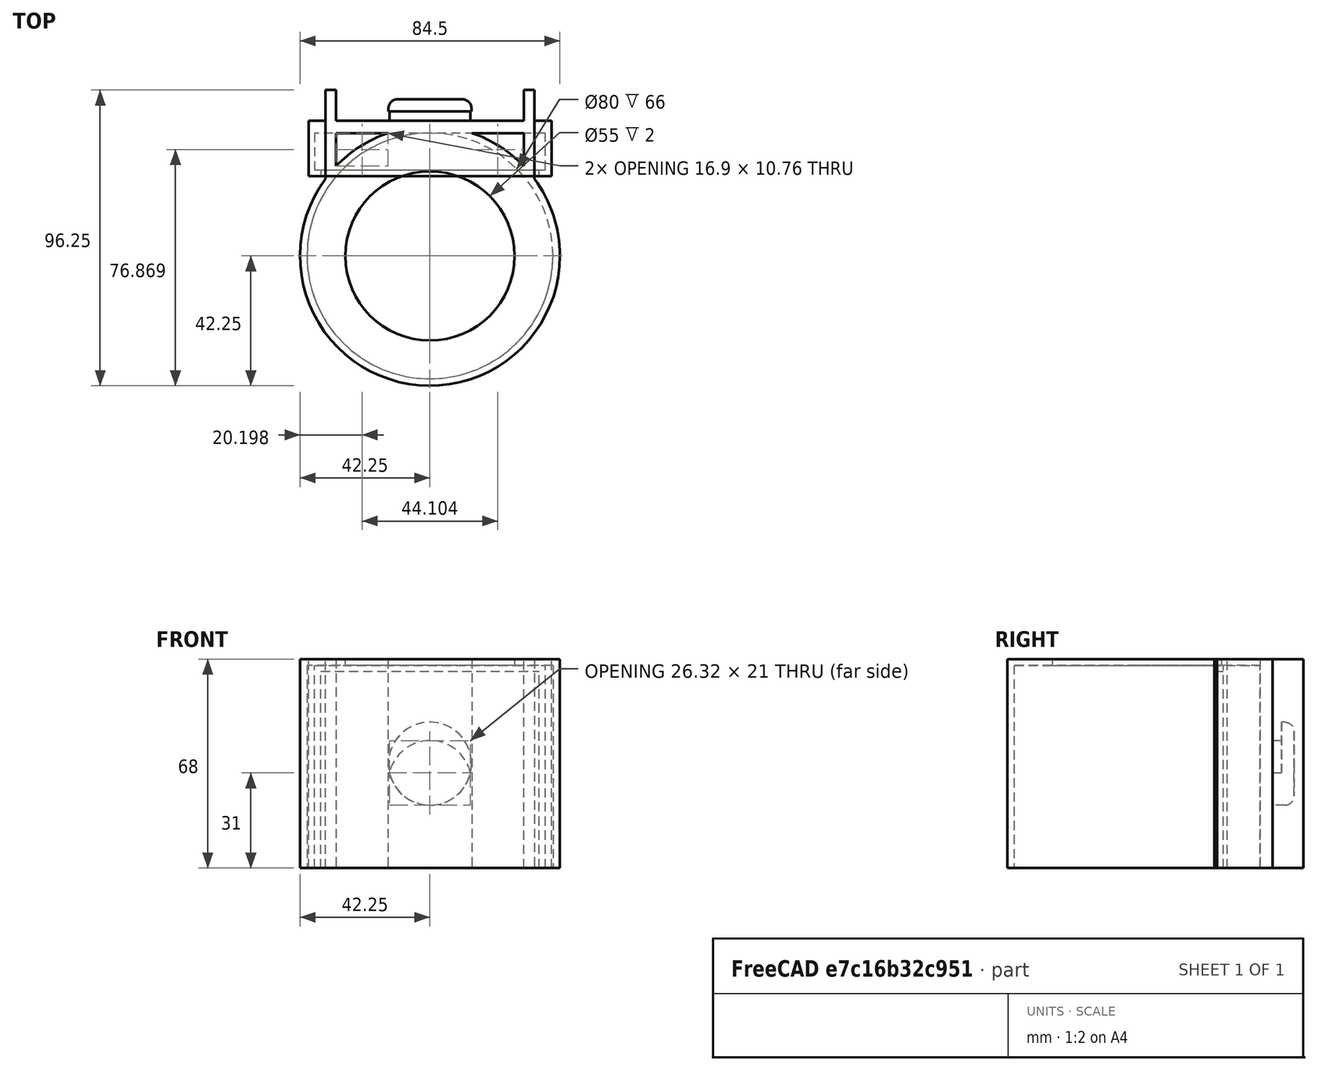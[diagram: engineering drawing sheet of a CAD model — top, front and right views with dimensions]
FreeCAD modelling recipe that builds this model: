
FCSTD DOCUMENT  (FreeCAD 1.0R39109 (Git))
Label: RackBaseAttachement
License: All rights reserved
LicenseURL: https://en.wikipedia.org/wiki/All_rights_reserved
objects: Sketcher::SketchObject×9, PartDesign::Pad×8, PartDesign::Body×3, PartDesign::Pocket×2, PartDesign::FeatureBase×2, Mesh::Feature×2, PartDesign::Fillet×1
note: 58 computed .brp shape members not serialized (recipe doc carries the construction recipe); baked Part::Feature solids carry a one-line shape summary decoded from their .brp

FEATURE [Sketcher::SketchObject] Sketch  label="BaseSketch"
  ArcFitTolerance = 1e-06
  AttachmentSupport = -> [XZ_Plane]
  FullyConstrained = true
  MakeInternals = false
  MapMode = 5
  Placement = pos=(0,0,0) rot=(1,0,0;1.5708rad)
  sketch-geometry (5):
    g0: LineSegment StartX=34 StartY=-34 StartZ=0 EndX=34 EndY=34 EndZ=0
    g1: LineSegment StartX=34 StartY=34 StartZ=0 EndX=-34 EndY=34 EndZ=0
    g2: LineSegment StartX=-34 StartY=34 StartZ=0 EndX=-34 EndY=-34 EndZ=0
    g3: LineSegment StartX=-34 StartY=-34 StartZ=0 EndX=34 EndY=-34 EndZ=0
    g4: GeomPoint [constr] X=0 Y=0 Z=0
  constraints (12):
    c: Coincident(g0,g1)
    c: Coincident(g1,g2)
    c: Coincident(g2,g3)
    c: Coincident(g3,g0)
    c: Vertical(g0)
    c: Vertical(g2)
    c: Horizontal(g1)
    c: Horizontal(g3)
    c: Symmetric(g2,g0,g4)
    c: Coincident(g4,g-1)
    c: DistanceX(g1,g1) = 68
    c: DistanceY(g2,g2) = 68
FEATURE [PartDesign::Pad] Pad  label="BasePad"
  Direction = (0,-1,2e-16)
  Length = 4
  Length2 = 10
  Placement = pos=(0,0,0) rot=(1,0,0;1.5708rad)
  Profile = -> Sketch
  ReferenceAxis = -> Sketch [N_Axis]
  Refine = true
  Suppressed = false
  Type = 0
FEATURE [Sketcher::SketchObject] Sketch001  label="ConnectorSketch"
  ArcFitTolerance = 1e-06
  AttachmentSupport = -> [Pad]
  ExternalGeometry = -> [Pad]
  FullyConstrained = true
  MakeInternals = false
  MapMode = 5
  Placement = pos=(0,0,0) rot=(-1,0,0;1.5708rad)
  sketch-geometry (9):
    g0: Circle CenterX=0 CenterY=0 CenterZ=0 NormalX=0 NormalY=0 NormalZ=1 AngleXU=0 Radius=13.5
    g1: LineSegment StartX=-34 StartY=-34 StartZ=0 EndX=-30.5 EndY=-34 EndZ=0
    g2: LineSegment StartX=-30.5 StartY=-34 StartZ=0 EndX=-30.5 EndY=34 EndZ=0
    g3: LineSegment StartX=-30.5 StartY=34 StartZ=0 EndX=-34 EndY=34 EndZ=0
    g4: LineSegment StartX=-34 StartY=34 StartZ=0 EndX=-34 EndY=-34 EndZ=0
    g5: LineSegment StartX=34 StartY=-34 StartZ=0 EndX=34 EndY=34 EndZ=0
    g6: LineSegment StartX=34 StartY=34 StartZ=0 EndX=30.5 EndY=34 EndZ=0
    g7: LineSegment StartX=30.5 StartY=34 StartZ=0 EndX=30.5 EndY=-34 EndZ=0
    g8: LineSegment StartX=30.5 StartY=-34 StartZ=0 EndX=34 EndY=-34 EndZ=0
  constraints (24):
    c: Diameter(g0) = 27
    c: Coincident(g0,g-1)
    c: Coincident(g1,g2)
    c: Coincident(g2,g3)
    c: Coincident(g3,g4)
    c: Coincident(g4,g1)
    c: Horizontal(g1)
    c: Horizontal(g3)
    c: Vertical(g2)
    c: Vertical(g4)
    c: Coincident(g1,g-4)
    c: PointOnObject(g2,g-3)
    c: Coincident(g5,g6)
    c: Coincident(g6,g7)
    c: Coincident(g7,g8)
    c: Coincident(g8,g5)
    c: Vertical(g5)
    c: Vertical(g7)
    c: Horizontal(g6)
    c: Horizontal(g8)
    c: Coincident(g5,g-4)
    c: PointOnObject(g6,g-3)
    c: Equal(g3,g6)
    c: DistanceX(g2,g6) = 61
FEATURE [PartDesign::Pad] Pad001  label="ConnectorPad"
  BaseFeature = -> Pad
  Direction = (0,1,2e-16)
  Length = 10
  Length2 = 10
  Placement = pos=(0,0,0) rot=(1,0,0;1.5708rad)
  Profile = -> Sketch001
  ReferenceAxis = -> Sketch001 [N_Axis]
  Refine = true
  Suppressed = false
  Type = 0
FEATURE [Sketcher::SketchObject] Sketch002  label="ConnectorGapSketch"
  ArcFitTolerance = 1e-06
  AttachmentSupport = -> [Pad001]
  ExternalGeometry = -> [Pad001]
  FullyConstrained = true
  MakeInternals = false
  MapMode = 5
  Placement = pos=(0,0,0) rot=(-1,0,0;1.5708rad)
  sketch-geometry (2):
    g0: ArcOfCircle CenterX=0 CenterY=0 CenterZ=0 NormalX=0 NormalY=0 NormalZ=1 AngleXU=0 Radius=13.5 StartAngle=2.9175 EndAngle=6.50728
    g1: ArcOfCircle CenterX=1e-16 CenterY=6 CenterZ=0 NormalX=0 NormalY=0 NormalZ=1 AngleXU=0 Radius=13.5 StartAngle=3.36569 EndAngle=6.05909
  constraints (7):
    c: Coincident(g0,g-1)
    c: Equal(g-3,g0)
    c: DistanceY(g0,g0) = 3
    c: Horizontal(g0,g0)
    c: Equal(g1,g-3)
    c: Coincident(g1,g0)
    c: Coincident(g1,g0)
FEATURE [PartDesign::Pocket] Pocket  label="ConnectorGapPocket"
  BaseFeature = -> Pad001
  Direction = (0,-1,-2e-16)
  Length = 3
  Length2 = 5
  Placement = pos=(0,0,0) rot=(1,0,0;1.5708rad)
  Profile = -> Sketch002
  ReferenceAxis = -> Sketch002 [N_Axis]
  Refine = true
  Reversed = true
  Suppressed = false
  Type = 0
FEATURE [PartDesign::Pocket] Pocket006
  BaseFeature = -> Pocket
  Direction = (0,-1,0)
  Length = 3
  Length2 = 5
  Placement = pos=(0,0,0) rot=(1,0,0;1.5708rad)
  Profile = -> Pocket [Face14]
  Refine = true
  Suppressed = false
  Type = 0
FEATURE [PartDesign::Fillet] Fillet
  Base = -> Pocket006 [Edge28]
  BaseFeature = -> Pocket006
  Placement = pos=(0,0,0) rot=(1,0,0;1.5708rad)
  Radius = 3
  Refine = true
  SupportTransform = false
  Suppressed = false
  UseAllEdges = false
FEATURE [PartDesign::Body] Body  label="RackAttachement"
  AllowCompound = false
  Group = -> [Sketch,Pad,Sketch001,Pad001,Sketch002,Pocket,Pocket006,Fillet]
  Origin = -> Origin
  Tip = -> Fillet
FEATURE [PartDesign::FeatureBase] Clone
  BaseFeature = -> Body
  Suppressed = false
FEATURE [Sketcher::SketchObject] Sketch016
  ArcFitTolerance = 1e-06
  AttachmentSupport = -> [XY_Plane005]
  ExternalGeometry = -> [Clone]
  FullyConstrained = true
  MakeInternals = false
  MapMode = 5
  sketch-geometry (3):
    g0: Circle CenterX=0 CenterY=-44 CenterZ=0 NormalX=0 NormalY=0 NormalZ=1 AngleXU=0 Radius=40
    g1: Circle CenterX=0 CenterY=-44 CenterZ=0 NormalX=0 NormalY=0 NormalZ=1 AngleXU=0 Radius=42.25
    g2: GeomPoint X=0 Y=-4 Z=0
  constraints (7):
    c: PointOnObject(g0,g-2)
    c: Coincident(g1,g0)
    c: Diameter(g1) = 84.5
    c: Diameter(g0) = 80
    c: PointOnObject(g2,g-2)
    c: PointOnObject(g2,g-3)
    c: PointOnObject(g2,g0)
FEATURE [PartDesign::Pad] Pad013
  BaseFeature = -> Clone
  Direction = (0,0,1)
  Length = 68
  Length2 = 10
  Midplane = true
  Profile = -> Sketch016
  ReferenceAxis = -> Sketch016 [N_Axis]
  Refine = true
  Suppressed = false
  Type = 0
FEATURE [Sketcher::SketchObject] Sketch017
  ArcFitTolerance = 1e-06
  AttachmentSupport = -> [Pad013]
  ExternalGeometry = -> [Pad013]
  FullyConstrained = true
  MakeInternals = false
  MapMode = 5
  Placement = pos=(0,0,34) rot=(0,0,1;0rad)
  sketch-geometry (2):
    g0: Circle CenterX=0 CenterY=-44 CenterZ=0 NormalX=0 NormalY=0 NormalZ=1 AngleXU=0 Radius=42.25
    g1: Circle CenterX=0 CenterY=-44 CenterZ=0 NormalX=0 NormalY=0 NormalZ=1 AngleXU=0 Radius=27.5
  constraints (4):
    c: Coincident(g0,g-3)
    c: Coincident(g1,g0)
    c: Equal(g0,g-3)
    c: Diameter(g1) = 55
FEATURE [PartDesign::Pad] Pad014
  BaseFeature = -> Pad013
  Direction = (0,0,1)
  Length = 2
  Length2 = 10
  Profile = -> Sketch017
  ReferenceAxis = -> Sketch017 [N_Axis]
  Refine = true
  Reversed = true
  Suppressed = false
  Type = 0
FEATURE [Sketcher::SketchObject] Sketch018
  ArcFitTolerance = 1e-06
  AttachmentSupport = -> [XY_Plane005]
  ExternalGeometry = -> [Pad014]
  FullyConstrained = true
  MakeInternals = false
  MapMode = 5
  sketch-geometry (8):
    g0: LineSegment StartX=-34 StartY=-4 StartZ=0 EndX=-34 EndY=-18.9189 EndZ=0
    g1: LineSegment StartX=-30.5 StartY=-14.7628 StartZ=0 EndX=-30.5 EndY=-4 EndZ=0
    g2: LineSegment StartX=-30.5 StartY=-4 StartZ=0 EndX=-34 EndY=-4 EndZ=0
    g3: LineSegment StartX=34 StartY=-4 StartZ=0 EndX=30.5 EndY=-4 EndZ=0
    g4: LineSegment StartX=34 StartY=-4 StartZ=0 EndX=34 EndY=-18.9189 EndZ=0
    g5: LineSegment StartX=30.5 StartY=-14.7628 StartZ=0 EndX=30.5 EndY=-4 EndZ=0
    g6: LineSegment StartX=-34 StartY=-18.9189 StartZ=0 EndX=-30.5 EndY=-14.7628 EndZ=0
    g7: LineSegment StartX=34 StartY=-18.9189 StartZ=0 EndX=30.5 EndY=-14.7628 EndZ=0
  constraints (22):
    c: Coincident(g0,g-3)
    c: PointOnObject(g0,g-6)
    c: Vertical(g0)
    c: PointOnObject(g1,g-3)
    c: Vertical(g1)
    c: Coincident(g2,g1)
    c: Coincident(g2,g0)
    c: Coincident(g3,g-4)
    c: PointOnObject(g3,g-4)
    c: Coincident(g4,g3)
    c: PointOnObject(g4,g-5)
    c: Vertical(g4)
    c: Coincident(g5,g3)
    c: Vertical(g5)
    c: PointOnObject(g5,g-5)
    c: DistanceX(g0,g1) = 3.5
    c: PointOnObject(g1,g-6)
    c: DistanceX(g3,g3) = 3.5
    c: Coincident(g6,g0)
    c: Coincident(g6,g1)
    c: Coincident(g7,g5)
    c: Coincident(g7,g4)
FEATURE [PartDesign::Pad] Pad015
  BaseFeature = -> Pad014
  Direction = (0,0,1)
  Length = 68
  Length2 = 10
  Midplane = true
  Profile = -> Sketch018
  ReferenceAxis = -> Sketch018 [N_Axis]
  Refine = true
  Suppressed = false
  Type = 0
FEATURE [PartDesign::Body] Body005  label="WaterBottleHolder"
  AllowCompound = false
  Group = -> [Clone,Sketch016,Pad013,Sketch017,Pad014,Sketch018,Pad015]
  Origin = -> Origin005
  Tip = -> Pad015
FEATURE [PartDesign::FeatureBase] Clone001
  BaseFeature = -> Body
  Suppressed = false
FEATURE [Sketcher::SketchObject] Sketch019
  ArcFitTolerance = 1e-06
  AttachmentSupport = -> [XY_Plane006]
  FullyConstrained = true
  MakeInternals = false
  MapMode = 5
  sketch-geometry (12):
    g0: LineSegment StartX=-39.5 StartY=0 StartZ=0 EndX=39.5 EndY=0 EndZ=0
    g1: LineSegment StartX=39.5 StartY=0 StartZ=0 EndX=39.5 EndY=-18 EndZ=0
    g2: LineSegment StartX=39.5 StartY=-18 StartZ=0 EndX=35.5 EndY=-18 EndZ=0
    g3: LineSegment StartX=35.5 StartY=-18 StartZ=0 EndX=35.5 EndY=-16 EndZ=0
    g4: LineSegment StartX=35.5 StartY=-16 StartZ=0 EndX=37.5 EndY=-16 EndZ=0
    g5: LineSegment StartX=37.5 StartY=-16 StartZ=0 EndX=37.5 EndY=-4 EndZ=0
    g6: LineSegment StartX=37.5 StartY=-4 StartZ=0 EndX=-37.5 EndY=-4 EndZ=0
    g7: LineSegment StartX=-37.5 StartY=-4 StartZ=0 EndX=-37.5 EndY=-16 EndZ=0
    g8: LineSegment StartX=-37.5 StartY=-16 StartZ=0 EndX=-35.5 EndY=-16 EndZ=0
    g9: LineSegment StartX=-35.5 StartY=-16 StartZ=0 EndX=-35.5 EndY=-18 EndZ=0
    g10: LineSegment StartX=-35.5 StartY=-18 StartZ=0 EndX=-39.5 EndY=-18 EndZ=0
    g11: LineSegment StartX=-39.5 StartY=-18 StartZ=0 EndX=-39.5 EndY=0 EndZ=0
  constraints (33):
    c: Horizontal(g0)
    c: Coincident(g0,g1)
    c: Vertical(g1)
    c: Coincident(g1,g2)
    c: Horizontal(g2)
    c: Coincident(g2,g3)
    c: Vertical(g3)
    c: Coincident(g3,g4)
    c: Horizontal(g4)
    c: Coincident(g4,g5)
    c: Vertical(g5)
    c: Coincident(g5,g6)
    c: Coincident(g6,g7)
    c: Vertical(g7)
    c: Coincident(g7,g8)
    c: Horizontal(g8)
    c: Coincident(g8,g9)
    c: Vertical(g9)
    c: Coincident(g9,g10)
    c: Horizontal(g10)
    c: Coincident(g10,g11)
    c: Coincident(g11,g0)
    c: Vertical(g11)
    c: Horizontal(g9,g2)
    c: Symmetric(g0,g0,g-1)
    c: Symmetric(g6,g5,g-2)
    c: Symmetric(g8,g3,g-2)
    c: DistanceY(g5,g0) = 4
    c: DistanceX(g5,g0) = 2
    c: DistanceY(g3,g3) = 2
    c: DistanceX(g4,g4) = 2
    c: DistanceX(g6,g6) = 75
    c: DistanceY(g5,g5) = 12
FEATURE [PartDesign::Pad] Pad016
  BaseFeature = -> Clone001
  Direction = (0,0,1)
  Length = 68
  Length2 = 10
  Midplane = true
  Profile = -> Sketch019
  ReferenceAxis = -> Sketch019 [N_Axis]
  Refine = true
  Suppressed = false
  Type = 0
FEATURE [Sketcher::SketchObject] Sketch020
  ArcFitTolerance = 1e-06
  AttachmentSupport = -> [Pad016]
  ExternalGeometry = -> [Pad016]
  FullyConstrained = true
  MakeInternals = false
  MapMode = 5
  Placement = pos=(0,0,34) rot=(0,0,1;0rad)
  sketch-geometry (4):
    g0: LineSegment StartX=-39.5 StartY=0 StartZ=0 EndX=-39.5 EndY=-18 EndZ=0
    g1: LineSegment StartX=-39.5 StartY=-18 StartZ=0 EndX=39.5 EndY=-18 EndZ=0
    g2: LineSegment StartX=39.5 StartY=-18 StartZ=0 EndX=39.5 EndY=0 EndZ=0
    g3: LineSegment StartX=39.5 StartY=0 StartZ=0 EndX=-39.5 EndY=0 EndZ=0
  constraints (10):
    c: Coincident(g0,g1)
    c: Coincident(g1,g2)
    c: Coincident(g2,g3)
    c: Coincident(g3,g0)
    c: Vertical(g0)
    c: Vertical(g2)
    c: Horizontal(g1)
    c: Horizontal(g3)
    c: Coincident(g0,g-3)
    c: Coincident(g1,g-4)
FEATURE [PartDesign::Pad] Pad017
  BaseFeature = -> Pad016
  Direction = (0,0,1)
  Length = 2
  Length2 = 10
  Profile = -> Sketch020
  ReferenceAxis = -> Sketch020 [N_Axis]
  Refine = true
  Reversed = true
  Suppressed = false
  Type = 0
FEATURE [Sketcher::SketchObject] Sketch021
  ArcFitTolerance = 1e-06
  AttachmentSupport = -> [Pad017]
  ExternalGeometry = -> [Pad017]
  FullyConstrained = true
  MakeInternals = false
  MapMode = 5
  Placement = pos=(0,0,32) rot=(1,0,0;3.14159rad)
  sketch-geometry (4):
    g0: LineSegment StartX=-35.5 StartY=16 StartZ=0 EndX=35.5 EndY=16 EndZ=0
    g1: LineSegment StartX=35.5 StartY=16 StartZ=0 EndX=35.5 EndY=18 EndZ=0
    g2: LineSegment StartX=35.5 StartY=18 StartZ=0 EndX=-35.5 EndY=18 EndZ=0
    g3: LineSegment StartX=-35.5 StartY=18 StartZ=0 EndX=-35.5 EndY=16 EndZ=0
  constraints (10):
    c: Coincident(g0,g1)
    c: Coincident(g1,g2)
    c: Coincident(g2,g3)
    c: Coincident(g3,g0)
    c: Horizontal(g0)
    c: Horizontal(g2)
    c: Vertical(g1)
    c: Vertical(g3)
    c: Coincident(g0,g-3)
    c: Coincident(g1,g-4)
FEATURE [PartDesign::Pad] Pad018
  BaseFeature = -> Pad017
  Direction = (0,0,-1)
  Length = 2
  Length2 = 10
  Profile = -> Sketch021
  ReferenceAxis = -> Sketch021 [N_Axis]
  Refine = true
  Suppressed = false
  Type = 0
FEATURE [PartDesign::Body] Body006  label="PhoneHolder"
  AllowCompound = false
  Group = -> [Clone001,Sketch019,Pad016,Sketch020,Pad017,Sketch021,Pad018]
  Origin = -> Origin006
  Tip = -> Pad018
FEATURE [Mesh::Feature] Mesh  label="WaterBottleHolder (Meshed)"
FEATURE [Mesh::Feature] Mesh001  label="PhoneHolder (Meshed)"
